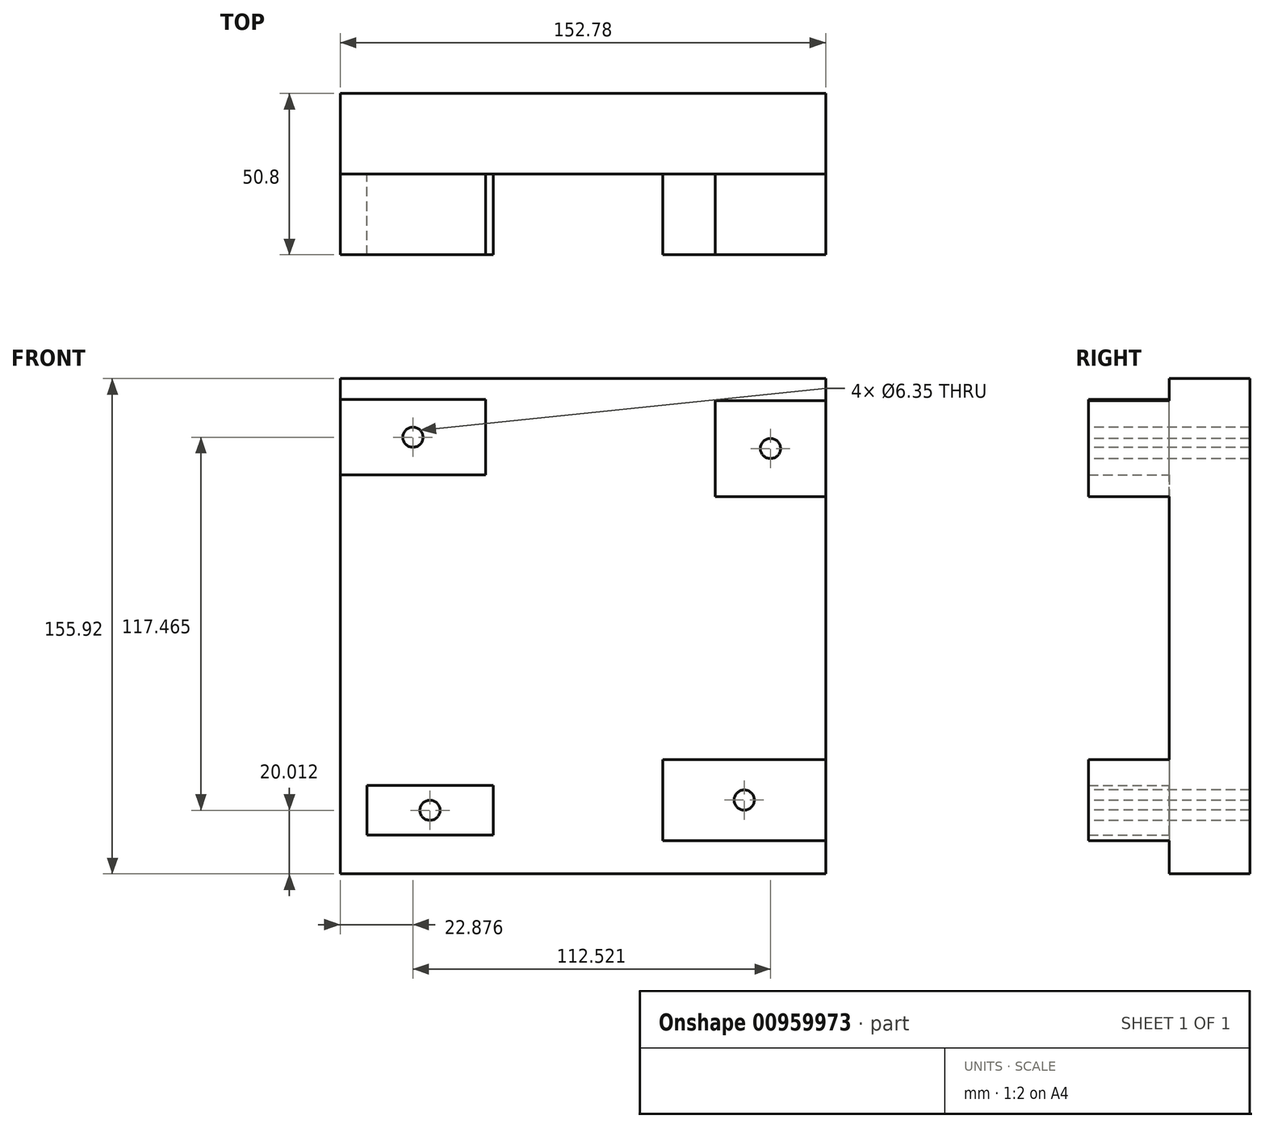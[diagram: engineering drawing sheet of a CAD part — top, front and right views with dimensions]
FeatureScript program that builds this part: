
annotation { "Feature Type Name" : "Feature", "Feature Type Description" : "" }
export const myFeature = defineFeature(function(context is Context, id is Id, definition is map)
    precondition{}
    {
        {
            var Q0;
            Q0=qCreatedBy(makeId("Front.planeOp"),FACE);
            var sketch = newSketch(context, id + "F0", { "sketchPlane" : qUnion([Q0])});
            skLineSegment(sketch, "E0.bottom", {"start": v(-76.39, 77.96) * mm, "end": v(76.39, 77.96) * mm});
            skLineSegment(sketch, "E0.top", {"start": v(-76.39, -77.96) * mm, "end": v(76.39, -77.96) * mm});
            skLineSegment(sketch, "E0.left", {"start": v(-76.39, 77.96) * mm, "end": v(-76.39, -77.96) * mm});
            skLineSegment(sketch, "E0.right", {"start": v(76.39, 77.96) * mm, "end": v(76.39, -77.96) * mm});
            skPoint(sketch, "E0.middle", {"position": v(0, 0) * mm});
            skSolve(sketch);
        }
        {
            var Q0;
            Q0=makeQuery(id+"F0.imprint","IMPRINT",FACE,{"disambiguationData":[TD([[makeQuery(id+"F0.imprint","IMPRINT",EDGE,{"derivedFrom":sQuery(id+"F0.wireOp",EDGE,"E0.bottom")}),-1.0]])]});
            extrude(context, id + "F1", {"entities" : qUnion([Q0]), "depth" : 25.4 * mm, "offsetDistance" : 25.4 * mm});
        }
        {
            var Q0;
            Q0=makeQuery(id+"F1.opExtrude","CAP_FACE",FACE,{"disambiguationData":[OSD([sQuery(id+"F0.wireOp",EDGE,"E0.bottom"),sQuery(id+"F0.wireOp",EDGE,"E0.top"),sQuery(id+"F0.wireOp",EDGE,"E0.left"),sQuery(id+"F0.wireOp",EDGE,"E0.right")])],"isStart":false});
            var sketch = newSketch(context, id + "F2", { "sketchPlane" : qUnion([Q0])});
            skPoint(sketch, "E1", {"position": v(-53.51, 59.52) * mm});
            skPoint(sketch, "E2", {"position": v(59, 55.97) * mm});
            skPoint(sketch, "E3", {"position": v(50.75, -54.75) * mm});
            skPoint(sketch, "E4", {"position": v(-48.15, -57.95) * mm});
            skSolve(sketch);
        }
        {
            var Q0;
            Q0=sQuery(id+"F2.wireOp",VERTEX,"E1");
            var Q1;
            Q1=sQuery(id+"F2.wireOp",VERTEX,"E2");
            var Q2;
            Q2=sQuery(id+"F2.wireOp",VERTEX,"E3");
            var Q3;
            Q3=sQuery(id+"F2.wireOp",VERTEX,"E4");
            var Q4;
            Q4=makeQuery(id+"F1.opExtrude","SWEPT_BODY",BODY,{"disambiguationData":[OSD([sQuery(id+"F0.wireOp",EDGE,"E0.bottom"),sQuery(id+"F0.wireOp",EDGE,"E0.top"),sQuery(id+"F0.wireOp",EDGE,"E0.left"),sQuery(id+"F0.wireOp",EDGE,"E0.right")])]});
            hole(context, id + "F3", {"style" : HoleStyle.SIMPLE, "endStyle" : HoleEndStyle.THROUGH, "holeDiameter" : 6.35 * mm, "majorDiameter" : 6.35 * mm, "isTappedThrough" : true, "tappedDepth" : 12.7 * mm, "tapClearance" : 3, "locations" : qUnion([Q0, Q1, Q2, Q3]), "scope" : qUnion([Q4])});
        }
        {
            var Q0;
            Q0=makeQuery(id+"F1.opExtrude","CAP_FACE",FACE,{"disambiguationData":[OSD([sQuery(id+"F0.wireOp",EDGE,"E0.bottom"),sQuery(id+"F0.wireOp",EDGE,"E0.top"),sQuery(id+"F0.wireOp",EDGE,"E0.left"),sQuery(id+"F0.wireOp",EDGE,"E0.right")])],"isStart":false});
            var sketch = newSketch(context, id + "F4", { "sketchPlane" : qUnion([Q0])});
            skLineSegment(sketch, "E5.bottom", {"start": v(-76.39, 47.63) * mm, "end": v(-30.64, 47.63) * mm});
            skLineSegment(sketch, "E5.top", {"start": v(-76.39, 71.4) * mm, "end": v(-30.64, 71.4) * mm});
            skLineSegment(sketch, "E5.left", {"start": v(-76.39, 47.63) * mm, "end": v(-76.39, 71.4) * mm});
            skLineSegment(sketch, "E5.right", {"start": v(-30.64, 47.63) * mm, "end": v(-30.64, 71.4) * mm});
            skPoint(sketch, "E5.middle", {"position": v(-53.51, 59.52) * mm});
            skLineSegment(sketch, "E6.bottom", {"start": v(-28.27, -65.79) * mm, "end": v(-68.02, -65.79) * mm});
            skLineSegment(sketch, "E6.top", {"start": v(-28.27, -50.1) * mm, "end": v(-68.02, -50.1) * mm});
            skLineSegment(sketch, "E6.left", {"start": v(-28.27, -65.79) * mm, "end": v(-28.27, -50.1) * mm});
            skLineSegment(sketch, "E6.right", {"start": v(-68.02, -65.79) * mm, "end": v(-68.02, -50.1) * mm});
            skPoint(sketch, "E6.middle", {"position": v(-48.15, -57.95) * mm});
            skLineSegment(sketch, "E7.bottom", {"start": v(76.39, 40.87) * mm, "end": v(41.63, 40.87) * mm});
            skLineSegment(sketch, "E7.top", {"start": v(76.39, 71.08) * mm, "end": v(41.63, 71.08) * mm});
            skLineSegment(sketch, "E7.left", {"start": v(76.39, 40.87) * mm, "end": v(76.39, 71.08) * mm});
            skLineSegment(sketch, "E7.right", {"start": v(41.63, 40.87) * mm, "end": v(41.63, 71.08) * mm});
            skPoint(sketch, "E7.middle", {"position": v(59, 55.97) * mm});
            skLineSegment(sketch, "E8.bottom", {"start": v(76.39, -41.95) * mm, "end": v(25.1, -41.95) * mm});
            skLineSegment(sketch, "E8.top", {"start": v(76.39, -67.55) * mm, "end": v(25.1, -67.55) * mm});
            skLineSegment(sketch, "E8.left", {"start": v(76.39, -41.95) * mm, "end": v(76.39, -67.55) * mm});
            skLineSegment(sketch, "E8.right", {"start": v(25.1, -41.95) * mm, "end": v(25.1, -67.55) * mm});
            skPoint(sketch, "E8.middle", {"position": v(50.75, -54.75) * mm});
            skSolve(sketch);
        }
        {
            var Q0;
            Q0=makeQuery(id+"F4.imprint","IMPRINT",FACE,{"disambiguationData":[TD([[makeQuery(id+"F4.imprint","IMPRINT",EDGE,{"derivedFrom":sQuery(id+"F4.wireOp",EDGE,"E5.bottom")}),1.0]])]});
            var Q1;
            Q1=makeQuery(id+"F4.imprint","IMPRINT",FACE,{"disambiguationData":[TD([[makeQuery(id+"F4.imprint","IMPRINT",EDGE,{"derivedFrom":sQuery(id+"F4.wireOp",EDGE,"E6.bottom")}),-1.0]])]});
            var Q2;
            Q2=makeQuery(id+"F4.imprint","IMPRINT",FACE,{"disambiguationData":[TD([[makeQuery(id+"F4.imprint","IMPRINT",EDGE,{"derivedFrom":sQuery(id+"F4.wireOp",EDGE,"E8.bottom")}),1.0]])]});
            var Q3;
            Q3=makeQuery(id+"F4.imprint","IMPRINT",FACE,{"disambiguationData":[TD([[makeQuery(id+"F4.imprint","IMPRINT",EDGE,{"derivedFrom":sQuery(id+"F4.wireOp",EDGE,"E7.bottom")}),-1.0]])]});
            extrude(context, id + "F5", {"entities" : qUnion([Q0, Q1, Q2, Q3]), "operationType" : NewBodyOperationType.ADD, "depth" : 25.4 * mm, "offsetDistance" : 25.4 * mm});
        }
    });
